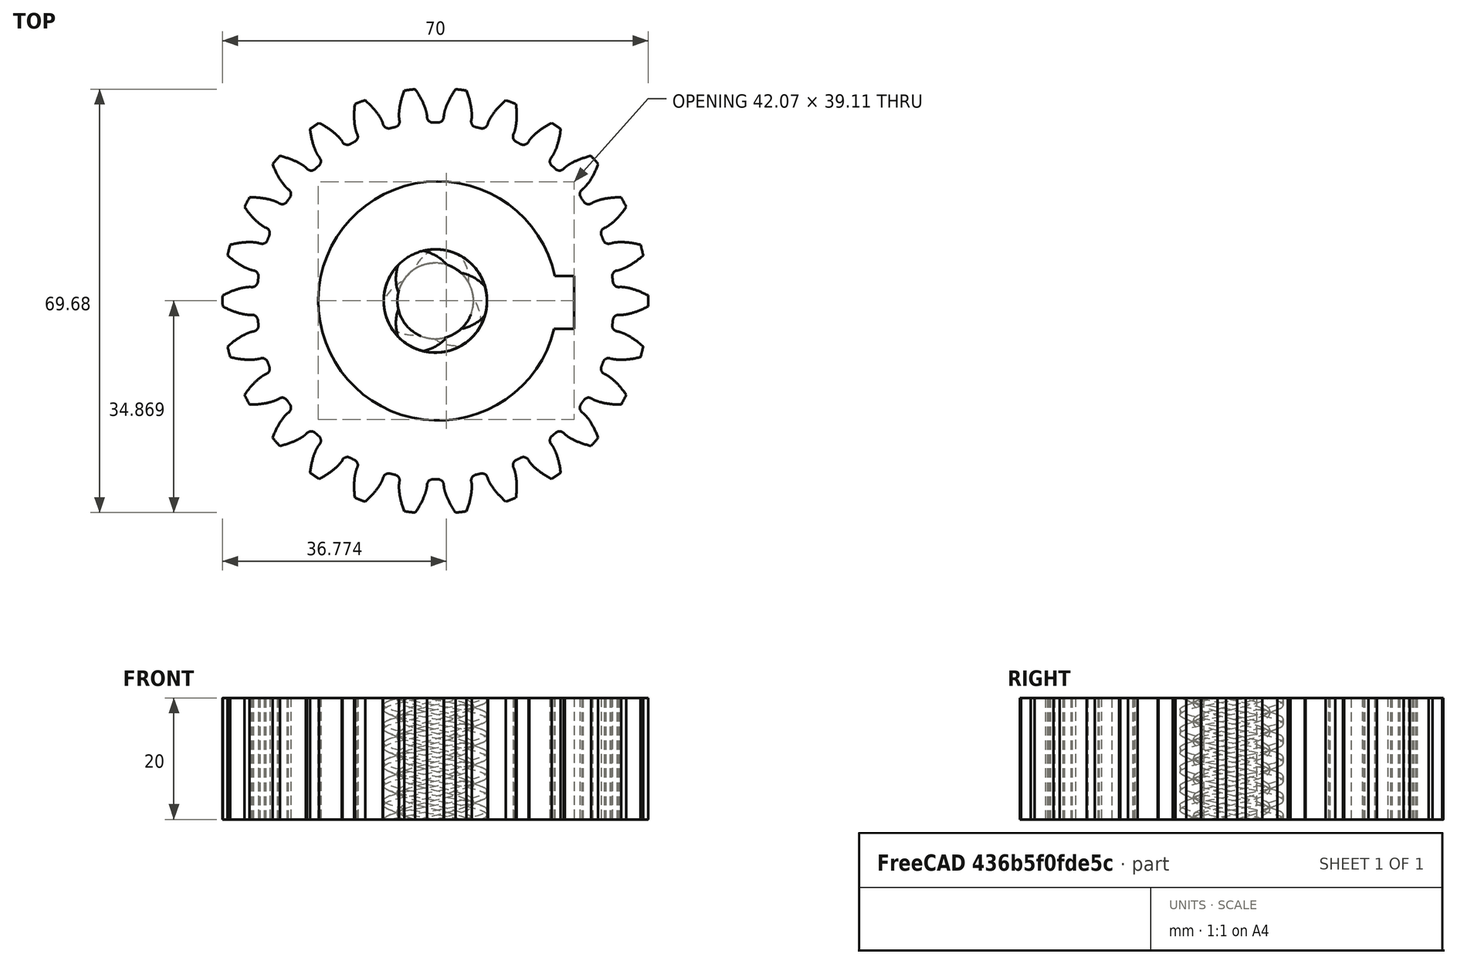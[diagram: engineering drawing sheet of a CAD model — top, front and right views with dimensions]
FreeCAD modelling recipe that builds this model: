
FCSTD DOCUMENT  (FreeCAD 1.2R20251230 (Git shallow))
Label: gear_1
License: Creative Commons Attribution 4.0
LicenseURL: https://creativecommons.org/licenses/by/4.0/
objects: App::Point×1, Part::Part2DObjectPython×1, PartDesign::Pad×1, Sketcher::SketchObject×1, PartDesign::Pocket×1, PartDesign::Body×1, Part::FeaturePython×1
note: 11 computed .brp shape members not serialized (recipe doc carries the construction recipe); baked Part::Feature solids carry a one-line shape summary decoded from their .brp

FEATURE [App::Point] Origin001  label="原点"
  Role = Origin
FEATURE [Part::Part2DObjectPython] InvoluteGear  # Draft 2D object (typed FeaturePython)
  AddendumCoefficient = 1
  DedendumCoefficient = 1.25
  ExternalGear = true
  HighPrecision = true
  Modules = 2.5
  NumberOfTeeth = 26
  PressureAngle = 20
  ProfileShiftCoefficient = 0
  RootFilletCoefficient = 0.38
FEATURE [PartDesign::Pad] Pad
  Direction = (0,0,1)
  Length = 20
  Length2 = 10
  Profile = -> InvoluteGear
  ReferenceAxis = -> InvoluteGear [N_Axis]
  Refine = true
  SideType = 0
  Suppressed = false
  Type = 0
  Type2 = 0
FEATURE [Sketcher::SketchObject] Sketch
  ArcFitTolerance = 1e-06
  AttachmentSupport = -> [Pad]
  ExternalTypes = [0]
  FullyConstrained = false
  MakeInternals = false
  MapMode = 5
  Placement = pos=(0,0,20) rot=(0,0,1;0rad)
  sketch-geometry (4):
    g0: ArcOfCircle CenterX=0.419323 CenterY=0 CenterZ=0 NormalX=0 NormalY=0 NormalZ=1 AngleXU=0 Radius=19.6814 StartAngle=0.210262 EndAngle=6.04662
    g1: LineSegment StartX=19.5525 StartY=-4.61266 StartZ=0 EndX=22.8075 EndY=-4.61266 EndZ=0
    g2: LineSegment StartX=22.8075 StartY=-4.61266 StartZ=0 EndX=22.8075 EndY=4.10782 EndZ=0
    g3: LineSegment StartX=22.8075 StartY=4.10782 StartZ=0 EndX=19.6672 EndY=4.10782 EndZ=0
  constraints (8):
    c: PointOnObject(g0,g-1)
    c: Coincident(g1,g2)
    c: Coincident(g2,g3)
    c: Vertical(g2)
    c: Horizontal(g3)
    c: Horizontal(g1)
    c: Coincident(g3,g0)
    c: Coincident(g1,g0)
FEATURE [PartDesign::Pocket] Pocket
  BaseFeature = -> Pad
  Direction = (0,0,-1)
  Length = 5
  Length2 = 5
  Profile = -> Sketch
  ReferenceAxis = -> Sketch [N_Axis]
  Refine = true
  SideType = 0
  Suppressed = false
  Type = 1
  Type2 = 0
FEATURE [PartDesign::Body] Body
  AllowCompound = true
  Group = -> [InvoluteGear,Pad,Sketch,Pocket]
  Origin = -> Origin
  Tip = -> Pocket
FEATURE [Part::FeaturePython] WormGear  # WARN: FeaturePython — macro-defined, semantics opaque (R4)
  AttacherType = Attacher::AttachEngine3D
  beta = 11.3099
  clearance = 0.25
  diameter = 15
  head = 0
  height = 20
  module = 1
  num_teeth = 3
  pressure_angle = 20
  reverse_pitch = false
  version = 1.3.0
